# Revit family: PRD_AR_MltFnctnDspnsrs_RODANPaperTowelSoapDispenserCombination_RODX601
name_source: partatom
category: Specialty Equipment
revit_build: Autodesk Revit 2018 (Build: 20190510_1515(x64)
units: mm (PartAtom-declared; Revit-internal decimal feet)

## family parameters
Cut with Voids When Loaded = Yes
Host = Face
OmniClass Number = 23.40.20.21.17
OmniClass Title = Paper Towel Dispensers, Disposal Units
Part Type = Normal
Room Calculation Point = No
Round Connector Dimension = Use Diameter
Shared = No

## types (1)
- RODX601
    AssetType = Fixed
    BIMObjectName = PRD_AR_MultiFunctionDispensers_RODANPaperTowelSoapDispenserCombination_RODX601
    Category = Pr_40_70_22_52, Multi-function dispensers
    CombinationPart1 = Paper towel dispenser
    CombinationPart2 = Soap dispenser
    Default Elevation = 800 mm  [stored 2.62467 ft]
    Description = Paper towel, soap dispenser combination for wall mounting, stainless steel, surface satin finished, material thickness 0.8 mm, cylinder lock with KWC standard key, inspection windows on sides, paper towel dispenser with loading capacity 300 - 400 pcs. of paper depending on convolution, suitable for liquid soaps and lotions, 0.8 liter soap tank, pull lever, includes stainless steel screws and dowels.
    DispenserMaterial = PRD_AR_StainlessSteel_SatinFinished
    DurationUnit = year
    Features = stainless steel, surface satin finished
    FillingQuantity1 = 400
    FillingQuantity1Uom = Pieces
    FillingQuantity2 = 0.8
    FillingQuantity2Uom = Liter
    Finish = satin finished
    GrossWeight = 4.16 kg
    IfcExportAs = IfcFurnitureType
    IfcExportType = USERDEFINED
    IntegralAccessories = incl. stainless steel screws and dowels
    IsBuiltIn = TRUE
    Lock1 = Key-lock
    Lock2 = Key-lock
    MainColor = stainless steel
    Manufacturer = KWC Group AG
    ManufacturerName = KWC Group AG
    ManufacturerURL = www.kwc.com
www.kwc.com
    Material = stainless steel
    MaterialCode = 1.4301
    MaterialThickness = 0.80 mm
    Model = RODX601
    ModelNumber = 2000101221
    ModelReference = RODX601
    NBSDescription = Multi-function dispensers
    NBSReference = 45-35-72/384
    Name = Paper Towel Soap Dispenser Combination RODX601
    NetWeight = 3.47 kg
    NominalDepth = 134 mm
    NominalHeight = 325 mm  [stored 1.06627 ft]
    NominalWidth = 358 mm  [stored 1.17454 ft]
    ProductInformation = https://pim.kwc.com
    Size = 358 x 325 x 134 mm
    TypeOfConsumable1 = Paper towel
    TypeOfConsumable2 = Liquid soap
    TypeOfFixing = Screw
    TypeOfMounting = Wall mounting
    URL = www.kwc.com
    Uniclass2015Code = Pr_40_70_22_52
    Uniclass2015Title = Multi-function dispensers
    Uniclass2015Version = Products v1.10
    Version = 1
    WarrantyDurationUnit = year

note: [stored X ft] marks values corroborated as IEEE doubles in the binary element streams (Revit-internal decimal feet)

## geometry (parser evidence)
native form markers: Sweep x5
no freeform markers — native parametric forms only
